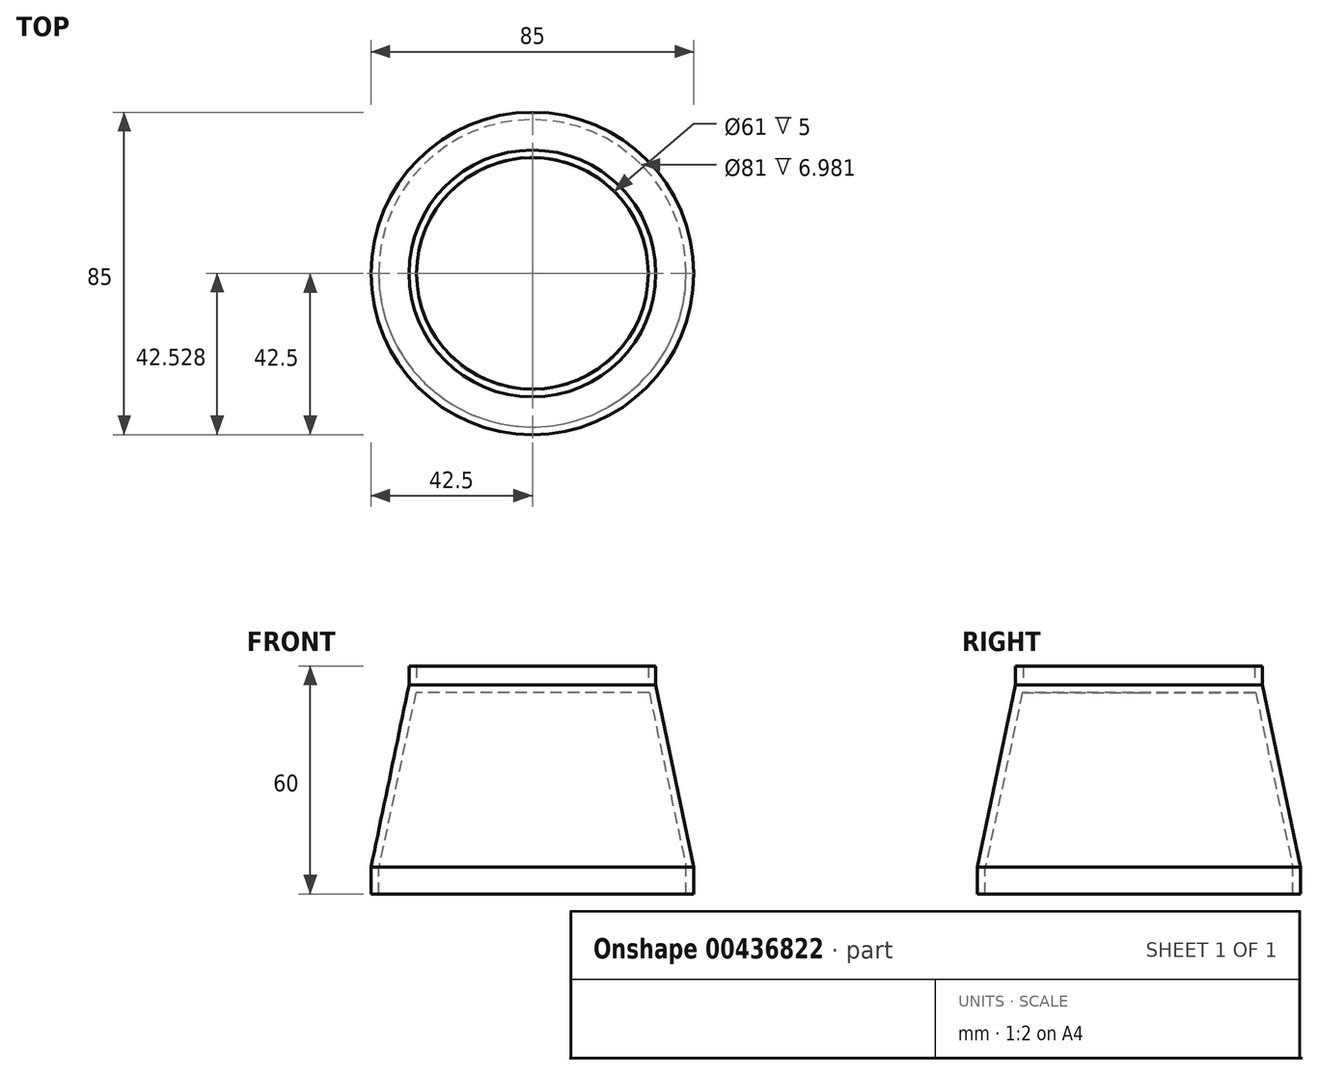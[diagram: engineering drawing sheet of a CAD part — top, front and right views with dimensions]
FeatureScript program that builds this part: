
annotation { "Feature Type Name" : "Feature", "Feature Type Description" : "" }
export const myFeature = defineFeature(function(context is Context, id is Id, definition is map)
    precondition{}
    {
        {
            var Q0;
            Q0=qCreatedBy(makeId("Right.planeOp"),FACE);
            var sketch = newSketch(context, id + "F0", { "sketchPlane" : qUnion([Q0])});
            skLineSegment(sketch, "E0", {"start": v(0, 0) * mm, "end": v(42.5, 0) * mm});
            skLineSegment(sketch, "E1", {"start": v(42.5, 0) * mm, "end": v(42.5, 7) * mm});
            skLineSegment(sketch, "E2", {"start": v(0, 0) * mm, "end": v(0, 55) * mm});
            skLineSegment(sketch, "E3", {"start": v(0, 55) * mm, "end": v(30.5, 55) * mm});
            skLineSegment(sketch, "E4", {"start": v(30.5, 55) * mm, "end": v(32.5, 55) * mm});
            skLineSegment(sketch, "E5", {"start": v(32.5, 55) * mm, "end": v(32.5, 60) * mm});
            skLineSegment(sketch, "E6", {"start": v(30.5, 55) * mm, "end": v(30.5, 60) * mm});
            skLineSegment(sketch, "E7", {"start": v(30.5, 60) * mm, "end": v(32.5, 60) * mm});
            skLineSegment(sketch, "E8", {"start": v(42.5, 7) * mm, "end": v(32.5, 55) * mm});
            skSolve(sketch);
        }
        {
            var Q0;
            Q0=makeQuery(id+"F0.imprint","IMPRINT",FACE,{"disambiguationData":[TD([[makeQuery(id+"F0.imprint","IMPRINT",EDGE,{"derivedFrom":sQuery(id+"F0.wireOp",EDGE,"E0")}),1.0]])]});
            var Q1;
            Q1=makeQuery(id+"F0.imprint","IMPRINT",FACE,{"disambiguationData":[TD([[makeQuery(id+"F0.imprint","IMPRINT",EDGE,{"derivedFrom":sQuery(id+"F0.wireOp",EDGE,"E4")}),1.0]])]});
            var Q2;
            Q2=sQuery(id+"F0.wireOp",EDGE,"E2");
            revolve(context, id + "F1", {"entities" : qUnion([Q0, Q1]), "axis" : qUnion([Q2]), "revolveType" : RevolveType.FULL});
        }
        {
            var Q0;
            Q0=qCreatedBy(makeId("Right.planeOp"),FACE);
            var sketch = newSketch(context, id + "F2", { "sketchPlane" : qUnion([Q0])});
            skLineSegment(sketch, "E9", {"start": v(0.03, -0.42) * mm, "end": v(40.53, -0.42) * mm});
            skLineSegment(sketch, "E10", {"start": v(40.53, -0.42) * mm, "end": v(40.53, 6.98) * mm});
            skLineSegment(sketch, "E11", {"start": v(0.03, -0.42) * mm, "end": v(0.03, 53.08) * mm});
            skLineSegment(sketch, "E12", {"start": v(0.03, 53.08) * mm, "end": v(30.76, 53.08) * mm});
            skLineSegment(sketch, "E13", {"start": v(30.76, 53.08) * mm, "end": v(40.53, 6.98) * mm});
            skSolve(sketch);
        }
        {
            var Q0;
            Q0 = qSketchRegion(id + "F2", true);
            var Q1;
            Q1=sQuery(id+"F2.wireOp",EDGE,"E11");
            revolve(context, id + "F3", {"operationType" : NewBodyOperationType.REMOVE, "entities" : qUnion([Q0]), "axis" : qUnion([Q1]), "revolveType" : RevolveType.FULL, "oppositeDirection" : true});
        }
    });
